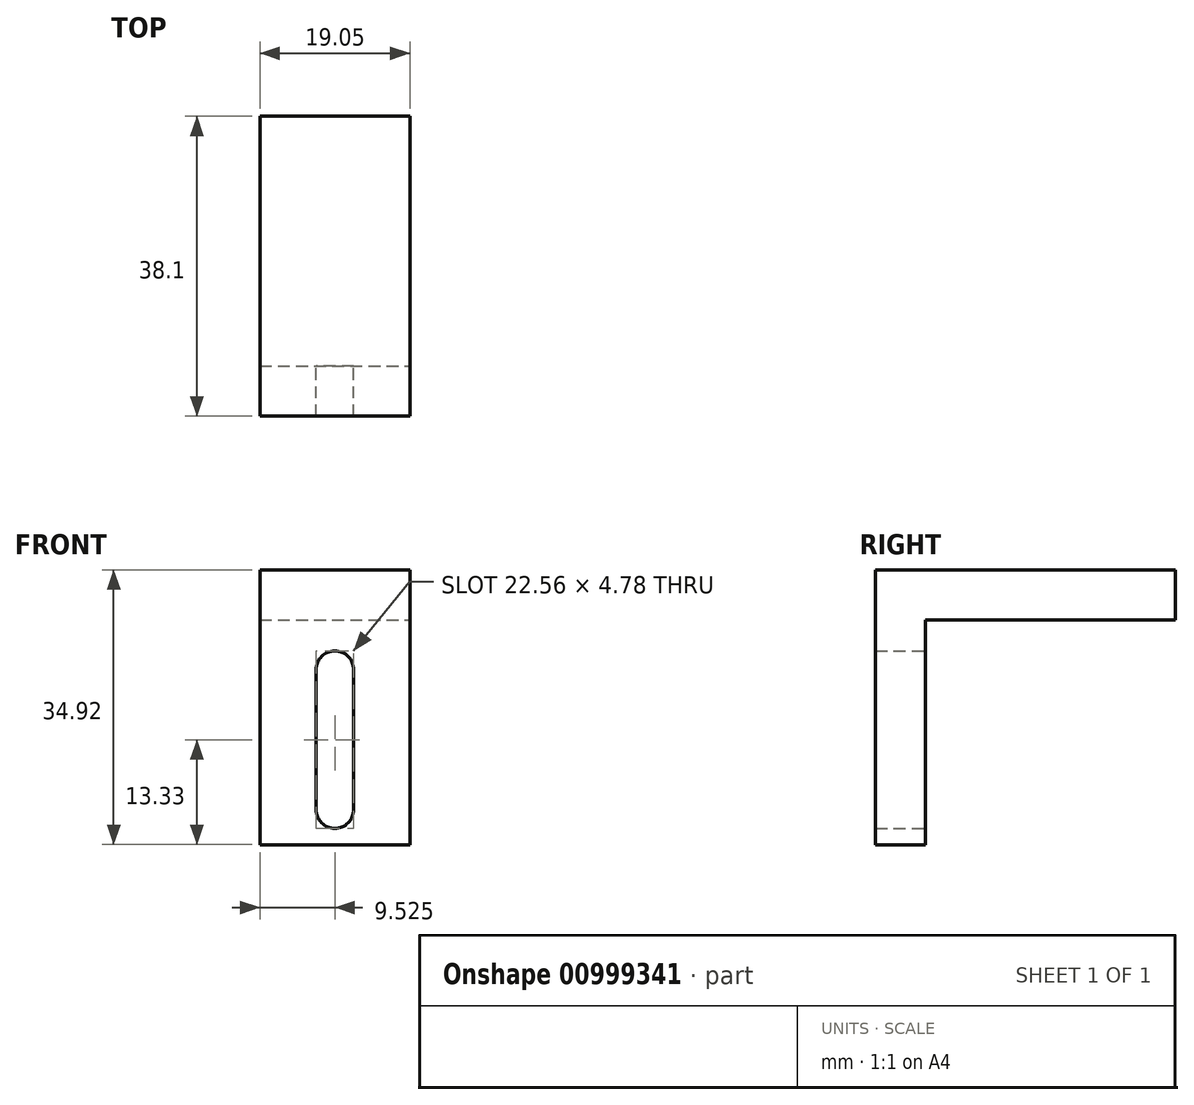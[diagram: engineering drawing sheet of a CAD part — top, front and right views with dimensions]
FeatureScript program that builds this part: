
annotation { "Feature Type Name" : "Feature", "Feature Type Description" : "" }
export const myFeature = defineFeature(function(context is Context, id is Id, definition is map)
    precondition{}
    {
        {
            var Q0;
            Q0=qCreatedBy(makeId("Front.planeOp"),FACE);
            var sketch = newSketch(context, id + "F0", { "sketchPlane" : qUnion([Q0])});
            skLineSegment(sketch, "E0.bottom", {"start": v(0, 0) * mm, "end": v(19.05, 0) * mm});
            skLineSegment(sketch, "E0.top", {"start": v(0, -34.93) * mm, "end": v(19.05, -34.93) * mm});
            skLineSegment(sketch, "E0.left", {"start": v(0, 0) * mm, "end": v(0, -34.93) * mm});
            skLineSegment(sketch, "E0.right", {"start": v(19.05, 0) * mm, "end": v(19.05, -34.93) * mm});
            skCircle(sketch, "E1", {"center": v(9.53, -12.7) * mm, "radius": 2.39 * mm});
            skCircle(sketch, "E2", {"center": v(9.53, -30.48) * mm, "radius": 2.39 * mm});
            skLineSegment(sketch, "E3", {"start": v(7.14, -12.7) * mm, "end": v(7.14, -30.48) * mm});
            skLineSegment(sketch, "E4", {"start": v(11.91, -12.7) * mm, "end": v(11.91, -30.48) * mm});
            skSolve(sketch);
        }
        {
            var Q0;
            Q0 = qSketchRegion(id + "F0", true);
            extrude(context, id + "F1", {"entities" : qUnion([Q0]), "depth" : 6.35 * mm, "offsetDistance" : 25.4 * mm});
        }
        {
            var Q0;
            Q0=makeQuery(id+"F1.opExtrude","CAP_FACE",FACE,{"disambiguationData":[OSD([sQuery(id+"F0.wireOp",EDGE,"E0.bottom"),sQuery(id+"F0.wireOp",EDGE,"E0.top"),sQuery(id+"F0.wireOp",EDGE,"E0.left"),sQuery(id+"F0.wireOp",EDGE,"E0.right"),sQuery(id+"F0.wireOp",EDGE,"E1"),sQuery(id+"F0.wireOp",EDGE,"E2"),sQuery(id+"F0.wireOp",EDGE,"E3"),sQuery(id+"F0.wireOp",EDGE,"E4")])],"isStart":true});
            var sketch = newSketch(context, id + "F2", { "sketchPlane" : qUnion([Q0])});
            skLineSegment(sketch, "E5.bottom", {"start": v(0, 0) * mm, "end": v(-19.05, 0) * mm});
            skLineSegment(sketch, "E5.top", {"start": v(0, -6.35) * mm, "end": v(-19.05, -6.35) * mm});
            skLineSegment(sketch, "E5.left", {"start": v(0, 0) * mm, "end": v(0, -6.35) * mm});
            skLineSegment(sketch, "E5.right", {"start": v(-19.05, 0) * mm, "end": v(-19.05, -6.35) * mm});
            skSolve(sketch);
        }
        {
            var Q0;
            Q0 = qSketchRegion(id + "F2", true);
            extrude(context, id + "F3", {"entities" : qUnion([Q0]), "operationType" : NewBodyOperationType.ADD, "depth" : 31.75 * mm, "offsetDistance" : 25.4 * mm});
        }
    });
